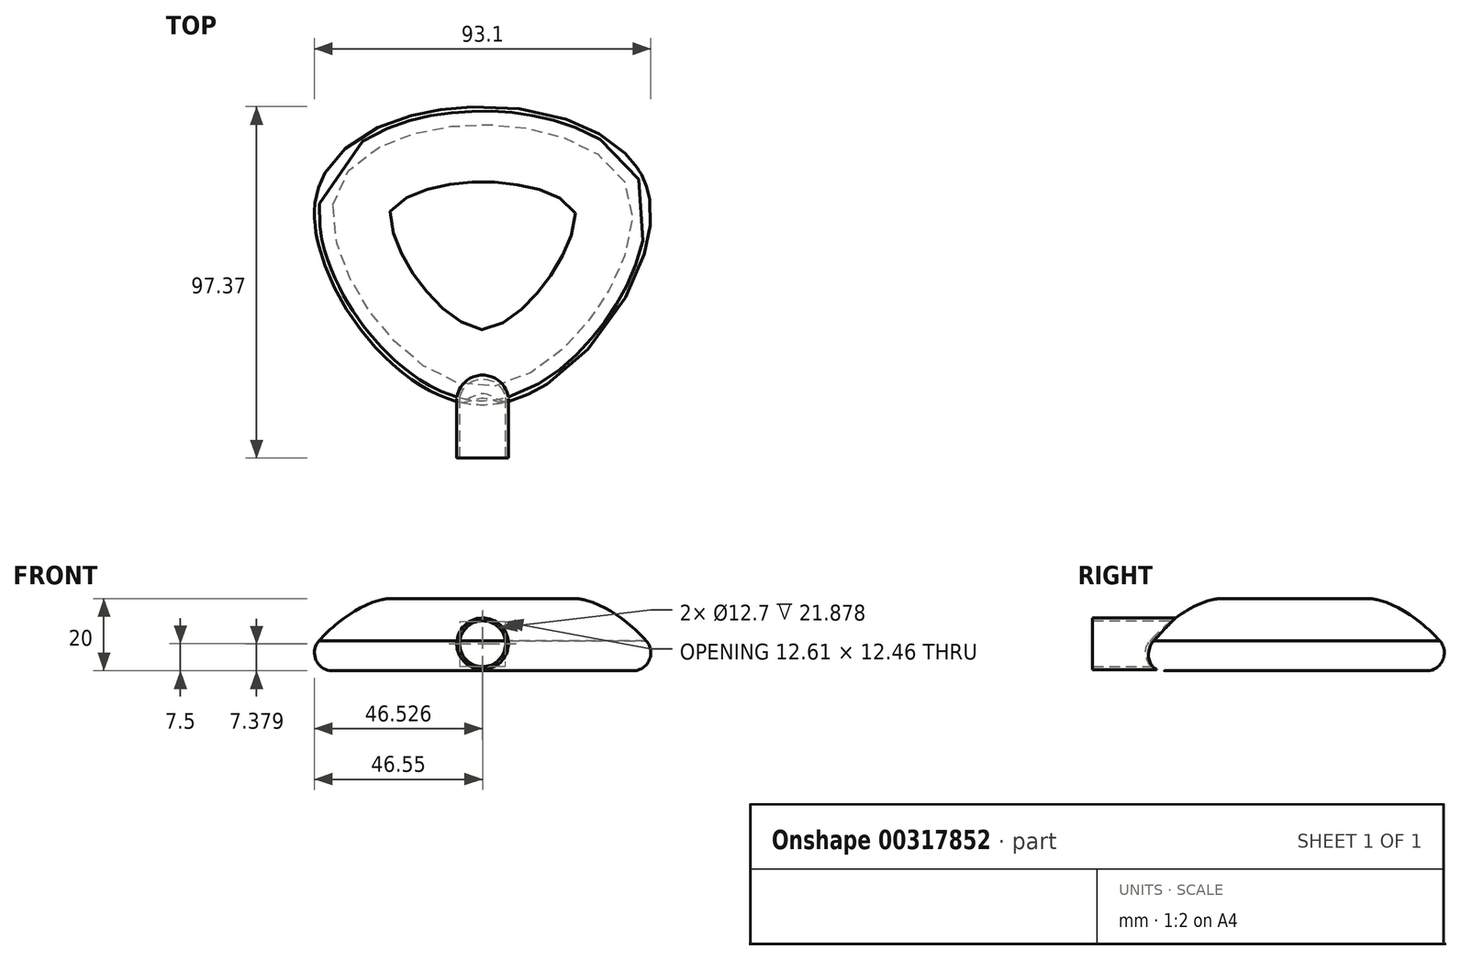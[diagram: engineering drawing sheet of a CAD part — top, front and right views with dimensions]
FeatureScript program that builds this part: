
annotation { "Feature Type Name" : "Feature", "Feature Type Description" : "" }
export const myFeature = defineFeature(function(context is Context, id is Id, definition is map)
    precondition{}
    {
        {
            var Q0;
            Q0=qCreatedBy(makeId("Top.planeOp"),FACE);
            var sketch = newSketch(context, id + "F0", { "sketchPlane" : qUnion([Q0])});
            skFitSpline(sketch, "E0", {"points": [v(-50, 0) * mm, v(0, 30) * mm, v(50, 0) * mm, v(0, -60) * mm, v(-50, 0) * mm]});
            skLineSegment(sketch, "E1", {"start": v(0, 55.54) * mm, "end": v(0, -67.7) * mm, "construction": true});
            skSolve(sketch);
        }
        {
            var Q0;
            Q0=makeQuery(id+"F0.imprint","IMPRINT",FACE,{"disambiguationData":[TD([[makeQuery(id+"F0.imprint","IMPRINT",EDGE,{"derivedFrom":sQuery(id+"F0.wireOp",EDGE,"E0")}),-1.0]])]});
            extrude(context, id + "F1", {"entities" : qUnion([Q0]), "depth" : 20 * mm});
        }
        {
            var Q0;
            Q0=makeQuery(id+"F1.opExtrude","CAP_FACE",FACE,{"disambiguationData":[OSD([sQuery(id+"F0.wireOp",EDGE,"E0")])],"isStart":false});
            fillet(context, id + "F2", {"entities" : qUnion([Q0]), "radius" : 25 * mm, "rho" : 0.3, "crossSection" : FilletCrossSection.CONIC, "allowEdgeOverflow" : false});
        }
        {
            var Q0;
            Q0=makeQuery(id+"F1.opExtrude","SWEPT_FACE",FACE,{"disambiguationData":[OSD([sQuery(id+"F0.wireOp",EDGE,"E0")])]});
            var Q1;
            Q1=makeQuery(id+"F1.opExtrude","CAP_FACE",FACE,{"disambiguationData":[OSD([sQuery(id+"F0.wireOp",EDGE,"E0")])],"isStart":true});
            fillet(context, id + "F3", {"entities" : qUnion([Q0, Q1]), "radius" : 5 * mm, "tangentPropagation" : true, "allowEdgeOverflow" : false});
        }
        {
            var Q0;
            Q0=qCreatedBy(makeId("Front.planeOp"),FACE);
            cPlane(context, id + "F4", {"entities" : qUnion([Q0]), "cplaneType" : CPlaneType.OFFSET, "offset" : 56 * mm, "width" : 150 * mm, "height" : 150 * mm});
        }
        {
            var Q0;
            Q0=qCreatedBy(id+"F4.planeOp",FACE);
            var sketch = newSketch(context, id + "F5", { "sketchPlane" : qUnion([Q0])});
            skCircle(sketch, "E2", {"center": v(0, 7.5) * mm, "radius": 7.14 * mm});
            skCircle(sketch, "E3", {"center": v(0, 7.5) * mm, "radius": 6.35 * mm});
            skSolve(sketch);
        }
        {
            var Q0;
            Q0=makeQuery(id+"F5.imprint","IMPRINT",FACE,{"disambiguationData":[TD([[makeQuery(id+"F5.imprint","IMPRINT",EDGE,{"derivedFrom":sQuery(id+"F5.wireOp",EDGE,"E2")}),1.0]])]});
            extrude(context, id + "F6", {"entities" : qUnion([Q0]), "operationType" : NewBodyOperationType.ADD, "depth" : 15 * mm, "hasSecondDirection" : true, "secondDirectionOppositeDirection" : true, "secondDirectionDepth" : 10 * mm});
        }
        {
            var Q0;
            Q0=makeQuery(id+"F1.opExtrude","SWEPT_BODY",BODY,{"disambiguationData":[OSD([sQuery(id+"F0.wireOp",EDGE,"E0")])]});
            transform(context, id + "F7", {"entities" : qUnion([Q0]), "transformType" : TransformType.TRANSLATION_3D, "dx" : 0 * mm, "dy" : 0 * mm, "dz" : 0 * mm, "makeCopy" : true});
        }
    });
